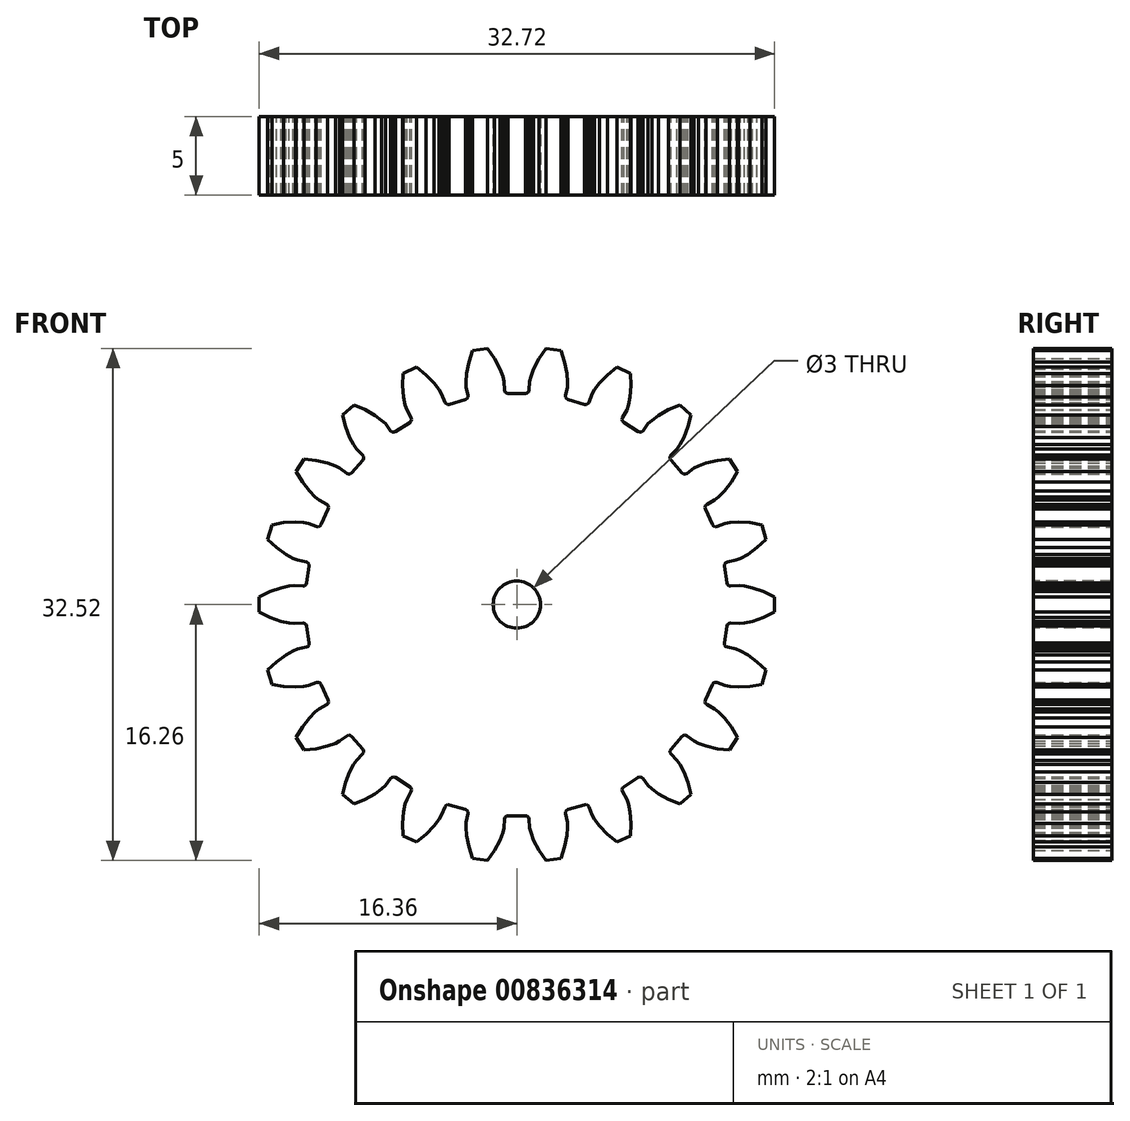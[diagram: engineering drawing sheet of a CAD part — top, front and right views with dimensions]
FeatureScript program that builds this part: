
annotation { "Feature Type Name" : "Feature", "Feature Type Description" : "" }
export const myFeature = defineFeature(function(context is Context, id is Id, definition is map)
    precondition{}
    {
        {
            var Q0;
            Q0=qCreatedBy(makeId("Front.planeOp"),FACE);
            var sketch = newSketch(context, id + "F0", { "sketchPlane" : qUnion([Q0])});
            skLineSegment(sketch, "E0", {"start": v(3.19, -14.67) * mm, "end": v(3.23, -14.15) * mm});
            skLineSegment(sketch, "E1", {"start": v(1.85, 16.26) * mm, "end": v(1.42, 15.62) * mm});
            skLineSegment(sketch, "E2", {"start": v(3.1, 13.28) * mm, "end": v(3.22, 13.83) * mm});
            skLineSegment(sketch, "E3", {"start": v(5.25, 14.06) * mm, "end": v(4.93, 13.65) * mm});
            skLineSegment(sketch, "E4", {"start": v(-9, -12.02) * mm, "end": v(-8.58, -11.7) * mm});
            skLineSegment(sketch, "E5", {"start": v(6.8, -11.58) * mm, "end": v(7.7, -10.99) * mm});
            skLineSegment(sketch, "E6", {"start": v(14.2, -2.94) * mm, "end": v(13.92, -2.82) * mm});
            skLineSegment(sketch, "E7", {"start": v(-0.54, 13.41) * mm, "end": v(-0.65, 13.44) * mm});
            skLineSegment(sketch, "E8", {"start": v(0.54, 13.41) * mm, "end": v(-0.54, 13.41) * mm});
            skLineSegment(sketch, "E9", {"start": v(-0.81, 14.18) * mm, "end": v(-0.89, 14.48) * mm});
            skLineSegment(sketch, "E10", {"start": v(-0.65, 13.44) * mm, "end": v(-0.74, 13.5) * mm});
            skLineSegment(sketch, "E11", {"start": v(-6.71, 11.66) * mm, "end": v(-6.8, 11.58) * mm});
            skLineSegment(sketch, "E12", {"start": v(0.81, 14.18) * mm, "end": v(0.77, 13.61) * mm});
            skLineSegment(sketch, "E13", {"start": v(-9.73, -9.3) * mm, "end": v(-9.73, -9.4) * mm});
            skLineSegment(sketch, "E14", {"start": v(3.1, 13.17) * mm, "end": v(3.1, 13.28) * mm});
            skLineSegment(sketch, "E15", {"start": v(4.57, 12.85) * mm, "end": v(4.51, 12.75) * mm});
            skLineSegment(sketch, "E16", {"start": v(0.89, 14.48) * mm, "end": v(0.81, 14.18) * mm});
            skLineSegment(sketch, "E17", {"start": v(-7.23, -14.68) * mm, "end": v(-6.36, -15.08) * mm});
            skLineSegment(sketch, "E18", {"start": v(-8.58, -11.7) * mm, "end": v(-8.35, -11.49) * mm});
            skLineSegment(sketch, "E19", {"start": v(-1.42, 15.62) * mm, "end": v(-1.85, 16.26) * mm});
            skLineSegment(sketch, "E20", {"start": v(-5.25, -14.06) * mm, "end": v(-4.93, -13.65) * mm});
            skLineSegment(sketch, "E21", {"start": v(3.04, 15.4) * mm, "end": v(2.8, 16.12) * mm});
            skLineSegment(sketch, "E22", {"start": v(-0.74, 13.5) * mm, "end": v(-0.77, 13.61) * mm});
            skLineSegment(sketch, "E23", {"start": v(14.07, -5.24) * mm, "end": v(14.8, -5.2) * mm});
            skLineSegment(sketch, "E24", {"start": v(-4.51, -12.75) * mm, "end": v(-4.41, -12.7) * mm});
            skLineSegment(sketch, "E25", {"start": v(-12.06, -6.36) * mm, "end": v(-12.56, -6.63) * mm});
            skLineSegment(sketch, "E26", {"start": v(-13.4, 1.27) * mm, "end": v(-13.48, 1.2) * mm});
            skLineSegment(sketch, "E27", {"start": v(-0.77, 13.61) * mm, "end": v(-0.81, 14.18) * mm});
            skLineSegment(sketch, "E28", {"start": v(-1.08, 14.97) * mm, "end": v(-1.42, 15.62) * mm});
            skLineSegment(sketch, "E29", {"start": v(-8, -11.04) * mm, "end": v(-7.92, -10.97) * mm});
            skLineSegment(sketch, "E30", {"start": v(-6.8, -11.58) * mm, "end": v(-6.71, -11.66) * mm});
            skLineSegment(sketch, "E31", {"start": v(-14.67, 3.2) * mm, "end": v(-14.2, 2.94) * mm});
            skLineSegment(sketch, "E32", {"start": v(-3.19, -14.67) * mm, "end": v(-3.04, -15.4) * mm});
            skLineSegment(sketch, "E33", {"start": v(0.54, -13.41) * mm, "end": v(0.65, -13.44) * mm});
            skLineSegment(sketch, "E34", {"start": v(-15.26, 3.63) * mm, "end": v(-14.67, 3.2) * mm});
            skLineSegment(sketch, "E35", {"start": v(-13.23, 5.15) * mm, "end": v(-13.54, 5.2) * mm});
            skLineSegment(sketch, "E36", {"start": v(-4.93, -13.65) * mm, "end": v(-4.77, -13.37) * mm});
            skLineSegment(sketch, "E37", {"start": v(-12.06, 6.36) * mm, "end": v(-11.98, 6.28) * mm});
            skLineSegment(sketch, "E38", {"start": v(-16.36, 0.48) * mm, "end": v(-16.36, -0.48) * mm});
            skLineSegment(sketch, "E39", {"start": v(-15.67, 0.82) * mm, "end": v(-16.36, 0.48) * mm});
            skLineSegment(sketch, "E40", {"start": v(3.19, 14.67) * mm, "end": v(3.04, 15.4) * mm});
            skLineSegment(sketch, "E41", {"start": v(3.23, 14.15) * mm, "end": v(3.19, 14.67) * mm});
            skLineSegment(sketch, "E42", {"start": v(3.22, 13.83) * mm, "end": v(3.23, 14.15) * mm});
            skLineSegment(sketch, "E43", {"start": v(-14.02, -8.44) * mm, "end": v(-13.5, -9.25) * mm});
            skLineSegment(sketch, "E44", {"start": v(-13.62, -7.78) * mm, "end": v(-14.02, -8.44) * mm});
            skLineSegment(sketch, "E45", {"start": v(-3.16, 13.08) * mm, "end": v(-3.26, 13.02) * mm});
            skLineSegment(sketch, "E46", {"start": v(-3.1, 13.17) * mm, "end": v(-3.16, 13.08) * mm});
            skLineSegment(sketch, "E47", {"start": v(-3.1, 13.28) * mm, "end": v(-3.1, 13.17) * mm});
            skLineSegment(sketch, "E48", {"start": v(-3.22, 13.83) * mm, "end": v(-3.1, 13.28) * mm});
            skLineSegment(sketch, "E49", {"start": v(-3.23, 14.15) * mm, "end": v(-3.22, 13.83) * mm});
            skLineSegment(sketch, "E50", {"start": v(-3.19, 14.67) * mm, "end": v(-3.23, 14.15) * mm});
            skLineSegment(sketch, "E51", {"start": v(-3.04, 15.4) * mm, "end": v(-3.19, 14.67) * mm});
            skLineSegment(sketch, "E52", {"start": v(-2.8, 16.12) * mm, "end": v(-3.04, 15.4) * mm});
            skLineSegment(sketch, "E53", {"start": v(-1.85, 16.26) * mm, "end": v(-2.8, 16.12) * mm});
            skLineSegment(sketch, "E54", {"start": v(5.76, 14.6) * mm, "end": v(5.25, 14.06) * mm});
            skLineSegment(sketch, "E55", {"start": v(6.36, 15.08) * mm, "end": v(5.76, 14.6) * mm});
            skLineSegment(sketch, "E56", {"start": v(7.23, 14.68) * mm, "end": v(6.36, 15.08) * mm});
            skLineSegment(sketch, "E57", {"start": v(-7.2, 13.18) * mm, "end": v(-7.08, 12.66) * mm});
            skLineSegment(sketch, "E58", {"start": v(-7.25, 13.91) * mm, "end": v(-7.2, 13.18) * mm});
            skLineSegment(sketch, "E59", {"start": v(-7.23, 14.68) * mm, "end": v(-7.25, 13.91) * mm});
            skLineSegment(sketch, "E60", {"start": v(-6.36, 15.08) * mm, "end": v(-7.23, 14.68) * mm});
            skLineSegment(sketch, "E61", {"start": v(-5.76, 14.6) * mm, "end": v(-6.36, 15.08) * mm});
            skLineSegment(sketch, "E62", {"start": v(-5.25, 14.06) * mm, "end": v(-5.76, 14.6) * mm});
            skLineSegment(sketch, "E63", {"start": v(-4.93, 13.65) * mm, "end": v(-5.25, 14.06) * mm});
            skLineSegment(sketch, "E64", {"start": v(-4.77, 13.37) * mm, "end": v(-4.93, 13.65) * mm});
            skLineSegment(sketch, "E65", {"start": v(-4.57, 12.85) * mm, "end": v(-4.77, 13.37) * mm});
            skLineSegment(sketch, "E66", {"start": v(-4.51, 12.75) * mm, "end": v(-4.57, 12.85) * mm});
            skLineSegment(sketch, "E67", {"start": v(1.42, 15.62) * mm, "end": v(1.08, 14.97) * mm});
            skLineSegment(sketch, "E68", {"start": v(-13.54, 5.2) * mm, "end": v(-14.07, 5.24) * mm});
            skLineSegment(sketch, "E69", {"start": v(-0.89, 14.48) * mm, "end": v(-1.08, 14.97) * mm});
            skLineSegment(sketch, "E70", {"start": v(13.17, -7.2) * mm, "end": v(12.8, -6.82) * mm});
            skLineSegment(sketch, "E71", {"start": v(2.8, 16.12) * mm, "end": v(1.85, 16.26) * mm});
            skLineSegment(sketch, "E72", {"start": v(-2.8, -16.12) * mm, "end": v(-1.85, -16.26) * mm});
            skLineSegment(sketch, "E73", {"start": v(-11.97, -6.07) * mm, "end": v(-11.95, -6.17) * mm});
            skLineSegment(sketch, "E74", {"start": v(-6.71, -11.87) * mm, "end": v(-6.98, -12.36) * mm});
            skLineSegment(sketch, "E75", {"start": v(-14.46, 1.18) * mm, "end": v(-14.97, 1.07) * mm});
            skLineSegment(sketch, "E76", {"start": v(-14.07, 5.24) * mm, "end": v(-14.8, 5.2) * mm});
            skLineSegment(sketch, "E77", {"start": v(-1.85, -16.26) * mm, "end": v(-1.42, -15.62) * mm});
            skLineSegment(sketch, "E78", {"start": v(-6.36, -15.08) * mm, "end": v(-5.76, -14.6) * mm});
            skLineSegment(sketch, "E79", {"start": v(-4.3, -12.72) * mm, "end": v(-4.41, -12.7) * mm});
            skLineSegment(sketch, "E80", {"start": v(-7.7, -10.99) * mm, "end": v(-7.81, -10.95) * mm});
            skLineSegment(sketch, "E81", {"start": v(7.23, 14.68) * mm, "end": v(7.25, 13.91) * mm});
            skLineSegment(sketch, "E82", {"start": v(0.74, -13.5) * mm, "end": v(0.77, -13.61) * mm});
            skLineSegment(sketch, "E83", {"start": v(-15.56, 5.07) * mm, "end": v(-14.8, 5.2) * mm});
            skLineSegment(sketch, "E84", {"start": v(-3.22, -13.83) * mm, "end": v(-3.23, -14.15) * mm});
            skLineSegment(sketch, "E85", {"start": v(-15.56, 5.07) * mm, "end": v(-15.83, 4.15) * mm});
            skLineSegment(sketch, "E86", {"start": v(-12.8, -6.82) * mm, "end": v(-13.17, -7.2) * mm});
            skLineSegment(sketch, "E87", {"start": v(-13.23, 5.15) * mm, "end": v(-12.7, 4.96) * mm});
            skLineSegment(sketch, "E88", {"start": v(-5.25, -14.06) * mm, "end": v(-5.76, -14.6) * mm});
            skLineSegment(sketch, "E89", {"start": v(-15.26, 3.63) * mm, "end": v(-15.83, 4.15) * mm});
            skLineSegment(sketch, "E90", {"start": v(13.5, -9.25) * mm, "end": v(12.74, -9.16) * mm});
            skLineSegment(sketch, "E91", {"start": v(-13.2, -2.56) * mm, "end": v(-13.27, -2.65) * mm});
            skLineSegment(sketch, "E92", {"start": v(-12.8, -6.82) * mm, "end": v(-12.56, -6.63) * mm});
            skLineSegment(sketch, "E93", {"start": v(-13.48, -1.2) * mm, "end": v(-13.59, -1.18) * mm});
            skLineSegment(sketch, "E94", {"start": v(-3.16, -13.08) * mm, "end": v(-3.1, -13.17) * mm});
            skLineSegment(sketch, "E95", {"start": v(-0.89, -14.48) * mm, "end": v(-1.08, -14.97) * mm});
            skLineSegment(sketch, "E96", {"start": v(11.53, -8.81) * mm, "end": v(11.24, -8.67) * mm});
            skLineSegment(sketch, "E97", {"start": v(-12.02, -9) * mm, "end": v(-12.74, -9.16) * mm});
            skLineSegment(sketch, "E98", {"start": v(-7.81, -10.95) * mm, "end": v(-7.92, -10.97) * mm});
            skLineSegment(sketch, "E99", {"start": v(-0.54, -13.41) * mm, "end": v(-0.65, -13.44) * mm});
            skLineSegment(sketch, "E100", {"start": v(9.64, -12.38) * mm, "end": v(9, -12.02) * mm});
            skLineSegment(sketch, "E101", {"start": v(-3.1, -13.28) * mm, "end": v(-3.22, -13.83) * mm});
            skLineSegment(sketch, "E102", {"start": v(-3.04, -15.4) * mm, "end": v(-2.8, -16.12) * mm});
            skLineSegment(sketch, "E103", {"start": v(-1.42, -15.62) * mm, "end": v(-1.08, -14.97) * mm});
            skLineSegment(sketch, "E104", {"start": v(-0.89, -14.48) * mm, "end": v(-0.81, -14.18) * mm});
            skLineSegment(sketch, "E105", {"start": v(-0.81, -14.18) * mm, "end": v(-0.77, -13.61) * mm});
            skLineSegment(sketch, "E106", {"start": v(-0.77, -13.61) * mm, "end": v(-0.74, -13.5) * mm});
            skLineSegment(sketch, "E107", {"start": v(-0.74, -13.5) * mm, "end": v(-0.65, -13.44) * mm});
            skLineSegment(sketch, "E108", {"start": v(-0.54, -13.41) * mm, "end": v(0.54, -13.41) * mm});
            skLineSegment(sketch, "E109", {"start": v(0.65, -13.44) * mm, "end": v(0.74, -13.5) * mm});
            skLineSegment(sketch, "E110", {"start": v(0.77, -13.61) * mm, "end": v(0.81, -14.18) * mm});
            skLineSegment(sketch, "E111", {"start": v(0.81, -14.18) * mm, "end": v(0.89, -14.48) * mm});
            skLineSegment(sketch, "E112", {"start": v(0.89, -14.48) * mm, "end": v(1.08, -14.97) * mm});
            skLineSegment(sketch, "E113", {"start": v(1.08, -14.97) * mm, "end": v(1.42, -15.62) * mm});
            skLineSegment(sketch, "E114", {"start": v(1.42, -15.62) * mm, "end": v(1.85, -16.26) * mm});
            skLineSegment(sketch, "E115", {"start": v(-15.26, -3.63) * mm, "end": v(-15.83, -4.15) * mm});
            skLineSegment(sketch, "E116", {"start": v(-15.83, -4.15) * mm, "end": v(-15.56, -5.07) * mm});
            skLineSegment(sketch, "E117", {"start": v(-15.56, -5.07) * mm, "end": v(-14.8, -5.2) * mm});
            skLineSegment(sketch, "E118", {"start": v(-14.67, -3.2) * mm, "end": v(-15.26, -3.63) * mm});
            skLineSegment(sketch, "E119", {"start": v(-14.8, -5.2) * mm, "end": v(-14.07, -5.24) * mm});
            skLineSegment(sketch, "E120", {"start": v(-14.2, -2.94) * mm, "end": v(-14.67, -3.2) * mm});
            skLineSegment(sketch, "E121", {"start": v(-13.92, -2.82) * mm, "end": v(-14.2, -2.94) * mm});
            skLineSegment(sketch, "E122", {"start": v(-14.07, -5.24) * mm, "end": v(-13.54, -5.2) * mm});
            skLineSegment(sketch, "E123", {"start": v(-13.37, -2.7) * mm, "end": v(-13.92, -2.82) * mm});
            skLineSegment(sketch, "E124", {"start": v(-13.54, -5.2) * mm, "end": v(-13.23, -5.15) * mm});
            skLineSegment(sketch, "E125", {"start": v(-13.27, -2.65) * mm, "end": v(-13.37, -2.7) * mm});
            skLineSegment(sketch, "E126", {"start": v(-13.23, -5.15) * mm, "end": v(-12.7, -4.96) * mm});
            skLineSegment(sketch, "E127", {"start": v(-13.2, -2.45) * mm, "end": v(-13.2, -2.56) * mm});
            skLineSegment(sketch, "E128", {"start": v(-13.17, -7.2) * mm, "end": v(-13.62, -7.78) * mm});
            skLineSegment(sketch, "E129", {"start": v(-13.5, -9.25) * mm, "end": v(-12.74, -9.16) * mm});
            skLineSegment(sketch, "E130", {"start": v(-11.98, -6.28) * mm, "end": v(-12.06, -6.36) * mm});
            skLineSegment(sketch, "E131", {"start": v(-12.02, -9) * mm, "end": v(-11.53, -8.81) * mm});
            skLineSegment(sketch, "E132", {"start": v(-11.95, -6.17) * mm, "end": v(-11.98, -6.28) * mm});
            skLineSegment(sketch, "E133", {"start": v(-10.88, -11.3) * mm, "end": v(-11.08, -12.05) * mm});
            skLineSegment(sketch, "E134", {"start": v(-11.08, -12.05) * mm, "end": v(-10.35, -12.68) * mm});
            skLineSegment(sketch, "E135", {"start": v(-10.61, -10.62) * mm, "end": v(-10.88, -11.3) * mm});
            skLineSegment(sketch, "E136", {"start": v(-10.36, -10.15) * mm, "end": v(-10.61, -10.62) * mm});
            skLineSegment(sketch, "E137", {"start": v(-10.18, -9.9) * mm, "end": v(-10.36, -10.15) * mm});
            skLineSegment(sketch, "E138", {"start": v(-10.35, -12.68) * mm, "end": v(-9.64, -12.38) * mm});
            skLineSegment(sketch, "E139", {"start": v(-9.79, -9.5) * mm, "end": v(-10.18, -9.9) * mm});
            skLineSegment(sketch, "E140", {"start": v(-9.73, -9.4) * mm, "end": v(-9.79, -9.5) * mm});
            skLineSegment(sketch, "E141", {"start": v(-7.2, -13.18) * mm, "end": v(-7.25, -13.91) * mm});
            skLineSegment(sketch, "E142", {"start": v(-7.25, -13.91) * mm, "end": v(-7.23, -14.68) * mm});
            skLineSegment(sketch, "E143", {"start": v(-7.08, -12.66) * mm, "end": v(-7.2, -13.18) * mm});
            skLineSegment(sketch, "E144", {"start": v(-6.98, -12.36) * mm, "end": v(-7.08, -12.66) * mm});
            skLineSegment(sketch, "E145", {"start": v(-6.69, -11.76) * mm, "end": v(-6.71, -11.87) * mm});
            skLineSegment(sketch, "E146", {"start": v(-3.23, -14.15) * mm, "end": v(-3.19, -14.67) * mm});
            skLineSegment(sketch, "E147", {"start": v(-7.08, 12.66) * mm, "end": v(-6.98, 12.36) * mm});
            skLineSegment(sketch, "E148", {"start": v(-6.98, 12.36) * mm, "end": v(-6.71, 11.87) * mm});
            skLineSegment(sketch, "E149", {"start": v(-6.71, 11.87) * mm, "end": v(-6.69, 11.76) * mm});
            skLineSegment(sketch, "E150", {"start": v(-4.77, -13.37) * mm, "end": v(-4.57, -12.85) * mm});
            skLineSegment(sketch, "E151", {"start": v(-4.57, -12.85) * mm, "end": v(-4.51, -12.75) * mm});
            skLineSegment(sketch, "E152", {"start": v(-4.41, 12.7) * mm, "end": v(-4.51, 12.75) * mm});
            skLineSegment(sketch, "E153", {"start": v(-4.3, 12.72) * mm, "end": v(-4.41, 12.7) * mm});
            skLineSegment(sketch, "E154", {"start": v(-4.3, -12.72) * mm, "end": v(-3.26, -13.02) * mm});
            skLineSegment(sketch, "E155", {"start": v(-3.26, 13.02) * mm, "end": v(-4.3, 12.72) * mm});
            skLineSegment(sketch, "E156", {"start": v(-3.26, -13.02) * mm, "end": v(-3.16, -13.08) * mm});
            skLineSegment(sketch, "E157", {"start": v(-3.1, -13.17) * mm, "end": v(-3.1, -13.28) * mm});
            skLineSegment(sketch, "E158", {"start": v(-10.35, 12.68) * mm, "end": v(-11.08, 12.05) * mm});
            skLineSegment(sketch, "E159", {"start": v(-11.08, 12.05) * mm, "end": v(-10.88, 11.3) * mm});
            skLineSegment(sketch, "E160", {"start": v(-10.88, 11.3) * mm, "end": v(-10.61, 10.62) * mm});
            skLineSegment(sketch, "E161", {"start": v(-10.61, 10.62) * mm, "end": v(-10.36, 10.15) * mm});
            skLineSegment(sketch, "E162", {"start": v(-10.36, 10.15) * mm, "end": v(-10.18, 9.9) * mm});
            skLineSegment(sketch, "E163", {"start": v(-9.64, 12.38) * mm, "end": v(-10.35, 12.68) * mm});
            skLineSegment(sketch, "E164", {"start": v(-10.18, 9.9) * mm, "end": v(-9.79, 9.5) * mm});
            skLineSegment(sketch, "E165", {"start": v(-9.79, 9.5) * mm, "end": v(-9.73, 9.4) * mm});
            skLineSegment(sketch, "E166", {"start": v(-9.73, 9.4) * mm, "end": v(-9.73, 9.3) * mm});
            skLineSegment(sketch, "E167", {"start": v(-9.64, -12.38) * mm, "end": v(-9, -12.02) * mm});
            skLineSegment(sketch, "E168", {"start": v(-9, 12.02) * mm, "end": v(-9.64, 12.38) * mm});
            skLineSegment(sketch, "E169", {"start": v(-8.58, 11.7) * mm, "end": v(-9, 12.02) * mm});
            skLineSegment(sketch, "E170", {"start": v(-8.35, 11.49) * mm, "end": v(-8.58, 11.7) * mm});
            skLineSegment(sketch, "E171", {"start": v(-8.35, -11.49) * mm, "end": v(-8, -11.04) * mm});
            skLineSegment(sketch, "E172", {"start": v(-8, 11.04) * mm, "end": v(-8.35, 11.49) * mm});
            skLineSegment(sketch, "E173", {"start": v(-7.92, 10.97) * mm, "end": v(-8, 11.04) * mm});
            skLineSegment(sketch, "E174", {"start": v(-7.81, 10.95) * mm, "end": v(-7.92, 10.97) * mm});
            skLineSegment(sketch, "E175", {"start": v(-7.7, 10.99) * mm, "end": v(-7.81, 10.95) * mm});
            skLineSegment(sketch, "E176", {"start": v(-7.7, -10.99) * mm, "end": v(-6.8, -11.58) * mm});
            skLineSegment(sketch, "E177", {"start": v(-6.8, 11.58) * mm, "end": v(-7.7, 10.99) * mm});
            skLineSegment(sketch, "E178", {"start": v(-6.71, -11.66) * mm, "end": v(-6.69, -11.76) * mm});
            skLineSegment(sketch, "E179", {"start": v(-6.69, 11.76) * mm, "end": v(-6.71, 11.66) * mm});
            skLineSegment(sketch, "E180", {"start": v(-13.5, 9.25) * mm, "end": v(-14.02, 8.44) * mm});
            skLineSegment(sketch, "E181", {"start": v(-14.02, 8.44) * mm, "end": v(-13.62, 7.78) * mm});
            skLineSegment(sketch, "E182", {"start": v(-13.62, 7.78) * mm, "end": v(-13.17, 7.2) * mm});
            skLineSegment(sketch, "E183", {"start": v(-12.74, 9.16) * mm, "end": v(-13.5, 9.25) * mm});
            skLineSegment(sketch, "E184", {"start": v(-13.17, 7.2) * mm, "end": v(-12.8, 6.82) * mm});
            skLineSegment(sketch, "E185", {"start": v(-12.8, 6.82) * mm, "end": v(-12.56, 6.63) * mm});
            skLineSegment(sketch, "E186", {"start": v(-12.02, 9) * mm, "end": v(-12.74, 9.16) * mm});
            skLineSegment(sketch, "E187", {"start": v(-12.56, 6.63) * mm, "end": v(-12.06, 6.36) * mm});
            skLineSegment(sketch, "E188", {"start": v(-11.53, 8.81) * mm, "end": v(-12.02, 9) * mm});
            skLineSegment(sketch, "E189", {"start": v(-11.98, 6.28) * mm, "end": v(-11.95, 6.17) * mm});
            skLineSegment(sketch, "E190", {"start": v(-11.53, -8.81) * mm, "end": v(-11.24, -8.67) * mm});
            skLineSegment(sketch, "E191", {"start": v(-11.24, 8.67) * mm, "end": v(-11.53, 8.81) * mm});
            skLineSegment(sketch, "E192", {"start": v(-11.24, -8.67) * mm, "end": v(-10.8, -8.33) * mm});
            skLineSegment(sketch, "E193", {"start": v(-10.8, 8.33) * mm, "end": v(-11.24, 8.67) * mm});
            skLineSegment(sketch, "E194", {"start": v(-10.8, -8.33) * mm, "end": v(-10.7, -8.3) * mm});
            skLineSegment(sketch, "E195", {"start": v(-10.7, 8.3) * mm, "end": v(-10.8, 8.33) * mm});
            skLineSegment(sketch, "E196", {"start": v(-10.7, -8.3) * mm, "end": v(-10.58, -8.3) * mm});
            skLineSegment(sketch, "E197", {"start": v(-10.58, 8.3) * mm, "end": v(-10.7, 8.3) * mm});
            skLineSegment(sketch, "E198", {"start": v(-10.58, -8.3) * mm, "end": v(-10.5, -8.37) * mm});
            skLineSegment(sketch, "E199", {"start": v(-10.5, 8.37) * mm, "end": v(-10.58, 8.3) * mm});
            skLineSegment(sketch, "E200", {"start": v(-10.5, -8.37) * mm, "end": v(-9.78, -9.2) * mm});
            skLineSegment(sketch, "E201", {"start": v(-9.78, 9.2) * mm, "end": v(-10.5, 8.37) * mm});
            skLineSegment(sketch, "E202", {"start": v(-9.78, -9.2) * mm, "end": v(-9.73, -9.3) * mm});
            skLineSegment(sketch, "E203", {"start": v(-9.73, 9.3) * mm, "end": v(-9.78, 9.2) * mm});
            skLineSegment(sketch, "E204", {"start": v(-14.2, 2.94) * mm, "end": v(-13.92, 2.82) * mm});
            skLineSegment(sketch, "E205", {"start": v(-13.92, 2.82) * mm, "end": v(-13.37, 2.7) * mm});
            skLineSegment(sketch, "E206", {"start": v(-13.37, 2.7) * mm, "end": v(-13.27, 2.65) * mm});
            skLineSegment(sketch, "E207", {"start": v(-13.27, 2.65) * mm, "end": v(-13.2, 2.56) * mm});
            skLineSegment(sketch, "E208", {"start": v(-13.2, 2.56) * mm, "end": v(-13.2, 2.45) * mm});
            skLineSegment(sketch, "E209", {"start": v(-12.7, -4.96) * mm, "end": v(-12.6, -4.94) * mm});
            skLineSegment(sketch, "E210", {"start": v(-12.6, 4.94) * mm, "end": v(-12.7, 4.96) * mm});
            skLineSegment(sketch, "E211", {"start": v(-12.6, -4.94) * mm, "end": v(-12.5, -4.99) * mm});
            skLineSegment(sketch, "E212", {"start": v(-12.5, 4.99) * mm, "end": v(-12.6, 4.94) * mm});
            skLineSegment(sketch, "E213", {"start": v(-12.5, -4.99) * mm, "end": v(-12.43, -5.08) * mm});
            skLineSegment(sketch, "E214", {"start": v(-12.43, 5.08) * mm, "end": v(-12.5, 4.99) * mm});
            skLineSegment(sketch, "E215", {"start": v(-12.43, -5.08) * mm, "end": v(-11.97, -6.07) * mm});
            skLineSegment(sketch, "E216", {"start": v(-11.97, 6.07) * mm, "end": v(-12.43, 5.08) * mm});
            skLineSegment(sketch, "E217", {"start": v(-11.95, 6.17) * mm, "end": v(-11.97, 6.07) * mm});
            skLineSegment(sketch, "E218", {"start": v(-16.36, -0.48) * mm, "end": v(-15.67, -0.82) * mm});
            skLineSegment(sketch, "E219", {"start": v(-15.67, -0.82) * mm, "end": v(-14.97, -1.07) * mm});
            skLineSegment(sketch, "E220", {"start": v(-14.97, 1.07) * mm, "end": v(-15.67, 0.82) * mm});
            skLineSegment(sketch, "E221", {"start": v(-14.97, -1.07) * mm, "end": v(-14.46, -1.18) * mm});
            skLineSegment(sketch, "E222", {"start": v(-14.46, -1.18) * mm, "end": v(-14.15, -1.22) * mm});
            skLineSegment(sketch, "E223", {"start": v(-14.15, 1.22) * mm, "end": v(-14.46, 1.18) * mm});
            skLineSegment(sketch, "E224", {"start": v(-14.15, -1.22) * mm, "end": v(-13.59, -1.18) * mm});
            skLineSegment(sketch, "E225", {"start": v(-13.59, 1.18) * mm, "end": v(-14.15, 1.22) * mm});
            skLineSegment(sketch, "E226", {"start": v(-13.48, 1.2) * mm, "end": v(-13.59, 1.18) * mm});
            skLineSegment(sketch, "E227", {"start": v(-13.48, -1.2) * mm, "end": v(-13.4, -1.27) * mm});
            skLineSegment(sketch, "E228", {"start": v(-13.4, -1.27) * mm, "end": v(-13.35, -1.37) * mm});
            skLineSegment(sketch, "E229", {"start": v(-13.35, 1.37) * mm, "end": v(-13.4, 1.27) * mm});
            skLineSegment(sketch, "E230", {"start": v(-13.35, -1.37) * mm, "end": v(-13.2, -2.45) * mm});
            skLineSegment(sketch, "E231", {"start": v(-13.2, 2.45) * mm, "end": v(-13.35, 1.37) * mm});
            skLineSegment(sketch, "E232", {"start": v(0.65, 13.44) * mm, "end": v(0.54, 13.41) * mm});
            skLineSegment(sketch, "E233", {"start": v(0.74, 13.5) * mm, "end": v(0.65, 13.44) * mm});
            skLineSegment(sketch, "E234", {"start": v(0.77, 13.61) * mm, "end": v(0.74, 13.5) * mm});
            skLineSegment(sketch, "E235", {"start": v(1.08, 14.97) * mm, "end": v(0.89, 14.48) * mm});
            skLineSegment(sketch, "E236", {"start": v(1.85, -16.26) * mm, "end": v(2.8, -16.12) * mm});
            skLineSegment(sketch, "E237", {"start": v(2.8, -16.12) * mm, "end": v(3.04, -15.4) * mm});
            skLineSegment(sketch, "E238", {"start": v(3.04, -15.4) * mm, "end": v(3.19, -14.67) * mm});
            skLineSegment(sketch, "E239", {"start": v(3.22, -13.83) * mm, "end": v(3.1, -13.28) * mm});
            skLineSegment(sketch, "E240", {"start": v(3.23, -14.15) * mm, "end": v(3.22, -13.83) * mm});
            skLineSegment(sketch, "E241", {"start": v(3.1, -13.28) * mm, "end": v(3.1, -13.17) * mm});
            skLineSegment(sketch, "E242", {"start": v(3.1, -13.17) * mm, "end": v(3.16, -13.08) * mm});
            skLineSegment(sketch, "E243", {"start": v(3.16, 13.08) * mm, "end": v(3.1, 13.17) * mm});
            skLineSegment(sketch, "E244", {"start": v(3.16, -13.08) * mm, "end": v(3.26, -13.02) * mm});
            skLineSegment(sketch, "E245", {"start": v(3.26, 13.02) * mm, "end": v(3.16, 13.08) * mm});
            skLineSegment(sketch, "E246", {"start": v(3.26, -13.02) * mm, "end": v(4.3, -12.72) * mm});
            skLineSegment(sketch, "E247", {"start": v(4.3, 12.72) * mm, "end": v(3.26, 13.02) * mm});
            skLineSegment(sketch, "E248", {"start": v(4.3, -12.72) * mm, "end": v(4.41, -12.7) * mm});
            skLineSegment(sketch, "E249", {"start": v(4.41, 12.7) * mm, "end": v(4.3, 12.72) * mm});
            skLineSegment(sketch, "E250", {"start": v(4.41, -12.7) * mm, "end": v(4.51, -12.75) * mm});
            skLineSegment(sketch, "E251", {"start": v(4.51, 12.75) * mm, "end": v(4.41, 12.7) * mm});
            skLineSegment(sketch, "E252", {"start": v(4.51, -12.75) * mm, "end": v(4.57, -12.85) * mm});
            skLineSegment(sketch, "E253", {"start": v(4.57, -12.85) * mm, "end": v(4.77, -13.37) * mm});
            skLineSegment(sketch, "E254", {"start": v(4.77, 13.37) * mm, "end": v(4.57, 12.85) * mm});
            skLineSegment(sketch, "E255", {"start": v(4.77, -13.37) * mm, "end": v(4.93, -13.65) * mm});
            skLineSegment(sketch, "E256", {"start": v(4.93, 13.65) * mm, "end": v(4.77, 13.37) * mm});
            skLineSegment(sketch, "E257", {"start": v(4.93, -13.65) * mm, "end": v(5.25, -14.06) * mm});
            skLineSegment(sketch, "E258", {"start": v(5.25, -14.06) * mm, "end": v(5.76, -14.6) * mm});
            skLineSegment(sketch, "E259", {"start": v(5.76, -14.6) * mm, "end": v(6.36, -15.08) * mm});
            skLineSegment(sketch, "E260", {"start": v(6.36, -15.08) * mm, "end": v(7.23, -14.68) * mm});
            skLineSegment(sketch, "E261", {"start": v(6.71, -11.87) * mm, "end": v(6.69, -11.76) * mm});
            skLineSegment(sketch, "E262", {"start": v(6.98, -12.36) * mm, "end": v(6.71, -11.87) * mm});
            skLineSegment(sketch, "E263", {"start": v(7.08, -12.66) * mm, "end": v(6.98, -12.36) * mm});
            skLineSegment(sketch, "E264", {"start": v(7.2, -13.18) * mm, "end": v(7.08, -12.66) * mm});
            skLineSegment(sketch, "E265", {"start": v(7.23, -14.68) * mm, "end": v(7.25, -13.91) * mm});
            skLineSegment(sketch, "E266", {"start": v(7.25, -13.91) * mm, "end": v(7.2, -13.18) * mm});
            skLineSegment(sketch, "E267", {"start": v(6.69, -11.76) * mm, "end": v(6.71, -11.66) * mm});
            skLineSegment(sketch, "E268", {"start": v(6.71, 11.66) * mm, "end": v(6.69, 11.76) * mm});
            skLineSegment(sketch, "E269", {"start": v(6.71, -11.66) * mm, "end": v(6.8, -11.58) * mm});
            skLineSegment(sketch, "E270", {"start": v(6.8, 11.58) * mm, "end": v(6.71, 11.66) * mm});
            skLineSegment(sketch, "E271", {"start": v(7.7, 10.99) * mm, "end": v(6.8, 11.58) * mm});
            skLineSegment(sketch, "E272", {"start": v(7.7, -10.99) * mm, "end": v(7.81, -10.95) * mm});
            skLineSegment(sketch, "E273", {"start": v(7.81, 10.95) * mm, "end": v(7.7, 10.99) * mm});
            skLineSegment(sketch, "E274", {"start": v(7.81, -10.95) * mm, "end": v(7.92, -10.97) * mm});
            skLineSegment(sketch, "E275", {"start": v(7.92, 10.97) * mm, "end": v(7.81, 10.95) * mm});
            skLineSegment(sketch, "E276", {"start": v(7.92, -10.97) * mm, "end": v(8, -11.04) * mm});
            skLineSegment(sketch, "E277", {"start": v(8, 11.04) * mm, "end": v(7.92, 10.97) * mm});
            skLineSegment(sketch, "E278", {"start": v(8, -11.04) * mm, "end": v(8.35, -11.49) * mm});
            skLineSegment(sketch, "E279", {"start": v(8.35, 11.49) * mm, "end": v(8, 11.04) * mm});
            skLineSegment(sketch, "E280", {"start": v(8.35, -11.49) * mm, "end": v(8.58, -11.7) * mm});
            skLineSegment(sketch, "E281", {"start": v(8.58, 11.7) * mm, "end": v(8.35, 11.49) * mm});
            skLineSegment(sketch, "E282", {"start": v(8.58, -11.7) * mm, "end": v(9, -12.02) * mm});
            skLineSegment(sketch, "E283", {"start": v(9, 12.02) * mm, "end": v(8.58, 11.7) * mm});
            skLineSegment(sketch, "E284", {"start": v(9.64, 12.38) * mm, "end": v(9, 12.02) * mm});
            skLineSegment(sketch, "E285", {"start": v(9.73, -9.4) * mm, "end": v(9.73, -9.3) * mm});
            skLineSegment(sketch, "E286", {"start": v(9.64, -12.38) * mm, "end": v(10.35, -12.68) * mm});
            skLineSegment(sketch, "E287", {"start": v(9.79, -9.5) * mm, "end": v(9.73, -9.4) * mm});
            skLineSegment(sketch, "E288", {"start": v(10.18, -9.9) * mm, "end": v(9.79, -9.5) * mm});
            skLineSegment(sketch, "E289", {"start": v(10.36, -10.15) * mm, "end": v(10.18, -9.9) * mm});
            skLineSegment(sketch, "E290", {"start": v(10.35, -12.68) * mm, "end": v(11.08, -12.05) * mm});
            skLineSegment(sketch, "E291", {"start": v(10.61, -10.62) * mm, "end": v(10.36, -10.15) * mm});
            skLineSegment(sketch, "E292", {"start": v(11.08, -12.05) * mm, "end": v(10.88, -11.3) * mm});
            skLineSegment(sketch, "E293", {"start": v(10.88, -11.3) * mm, "end": v(10.61, -10.62) * mm});
            skLineSegment(sketch, "E294", {"start": v(9.73, -9.3) * mm, "end": v(9.78, -9.2) * mm});
            skLineSegment(sketch, "E295", {"start": v(9.78, 9.2) * mm, "end": v(9.73, 9.3) * mm});
            skLineSegment(sketch, "E296", {"start": v(9.78, -9.2) * mm, "end": v(10.5, -8.37) * mm});
            skLineSegment(sketch, "E297", {"start": v(10.5, 8.37) * mm, "end": v(9.78, 9.2) * mm});
            skLineSegment(sketch, "E298", {"start": v(10.5, -8.37) * mm, "end": v(10.58, -8.3) * mm});
            skLineSegment(sketch, "E299", {"start": v(10.58, 8.3) * mm, "end": v(10.5, 8.37) * mm});
            skLineSegment(sketch, "E300", {"start": v(10.58, -8.3) * mm, "end": v(10.7, -8.3) * mm});
            skLineSegment(sketch, "E301", {"start": v(10.7, 8.3) * mm, "end": v(10.58, 8.3) * mm});
            skLineSegment(sketch, "E302", {"start": v(10.7, -8.3) * mm, "end": v(10.8, -8.33) * mm});
            skLineSegment(sketch, "E303", {"start": v(10.8, 8.33) * mm, "end": v(10.7, 8.3) * mm});
            skLineSegment(sketch, "E304", {"start": v(10.8, -8.33) * mm, "end": v(11.24, -8.67) * mm});
            skLineSegment(sketch, "E305", {"start": v(11.24, 8.67) * mm, "end": v(10.8, 8.33) * mm});
            skLineSegment(sketch, "E306", {"start": v(11.53, 8.81) * mm, "end": v(11.24, 8.67) * mm});
            skLineSegment(sketch, "E307", {"start": v(11.53, -8.81) * mm, "end": v(12.02, -9) * mm});
            skLineSegment(sketch, "E308", {"start": v(11.98, -6.28) * mm, "end": v(11.95, -6.17) * mm});
            skLineSegment(sketch, "E309", {"start": v(12.06, -6.36) * mm, "end": v(11.98, -6.28) * mm});
            skLineSegment(sketch, "E310", {"start": v(12.02, -9) * mm, "end": v(12.74, -9.16) * mm});
            skLineSegment(sketch, "E311", {"start": v(12.56, -6.63) * mm, "end": v(12.06, -6.36) * mm});
            skLineSegment(sketch, "E312", {"start": v(12.8, -6.82) * mm, "end": v(12.56, -6.63) * mm});
            skLineSegment(sketch, "E313", {"start": v(13.62, -7.78) * mm, "end": v(13.17, -7.2) * mm});
            skLineSegment(sketch, "E314", {"start": v(13.5, -9.25) * mm, "end": v(14.02, -8.44) * mm});
            skLineSegment(sketch, "E315", {"start": v(14.02, -8.44) * mm, "end": v(13.62, -7.78) * mm});
            skLineSegment(sketch, "E316", {"start": v(11.95, -6.17) * mm, "end": v(11.97, -6.07) * mm});
            skLineSegment(sketch, "E317", {"start": v(11.97, 6.07) * mm, "end": v(11.95, 6.17) * mm});
            skLineSegment(sketch, "E318", {"start": v(11.97, -6.07) * mm, "end": v(12.43, -5.08) * mm});
            skLineSegment(sketch, "E319", {"start": v(12.43, 5.08) * mm, "end": v(11.97, 6.07) * mm});
            skLineSegment(sketch, "E320", {"start": v(12.43, -5.08) * mm, "end": v(12.5, -4.99) * mm});
            skLineSegment(sketch, "E321", {"start": v(12.5, 4.99) * mm, "end": v(12.43, 5.08) * mm});
            skLineSegment(sketch, "E322", {"start": v(12.5, -4.99) * mm, "end": v(12.6, -4.94) * mm});
            skLineSegment(sketch, "E323", {"start": v(12.6, 4.94) * mm, "end": v(12.5, 4.99) * mm});
            skLineSegment(sketch, "E324", {"start": v(12.6, -4.94) * mm, "end": v(12.7, -4.96) * mm});
            skLineSegment(sketch, "E325", {"start": v(12.7, 4.96) * mm, "end": v(12.6, 4.94) * mm});
            skLineSegment(sketch, "E326", {"start": v(12.7, -4.96) * mm, "end": v(13.23, -5.15) * mm});
            skLineSegment(sketch, "E327", {"start": v(13.2, -2.56) * mm, "end": v(13.2, -2.45) * mm});
            skLineSegment(sketch, "E328", {"start": v(13.27, -2.65) * mm, "end": v(13.2, -2.56) * mm});
            skLineSegment(sketch, "E329", {"start": v(13.23, -5.15) * mm, "end": v(13.54, -5.2) * mm});
            skLineSegment(sketch, "E330", {"start": v(13.37, -2.7) * mm, "end": v(13.27, -2.65) * mm});
            skLineSegment(sketch, "E331", {"start": v(13.92, -2.82) * mm, "end": v(13.37, -2.7) * mm});
            skLineSegment(sketch, "E332", {"start": v(13.54, -5.2) * mm, "end": v(14.07, -5.24) * mm});
            skLineSegment(sketch, "E333", {"start": v(14.67, -3.2) * mm, "end": v(14.2, -2.94) * mm});
            skLineSegment(sketch, "E334", {"start": v(15.26, -3.63) * mm, "end": v(14.67, -3.2) * mm});
            skLineSegment(sketch, "E335", {"start": v(14.8, -5.2) * mm, "end": v(15.56, -5.07) * mm});
            skLineSegment(sketch, "E336", {"start": v(15.56, -5.07) * mm, "end": v(15.83, -4.15) * mm});
            skLineSegment(sketch, "E337", {"start": v(15.83, -4.15) * mm, "end": v(15.26, -3.63) * mm});
            skLineSegment(sketch, "E338", {"start": v(13.2, -2.45) * mm, "end": v(13.35, -1.37) * mm});
            skLineSegment(sketch, "E339", {"start": v(13.35, 1.37) * mm, "end": v(13.2, 2.45) * mm});
            skLineSegment(sketch, "E340", {"start": v(13.35, -1.37) * mm, "end": v(13.4, -1.27) * mm});
            skLineSegment(sketch, "E341", {"start": v(13.4, 1.27) * mm, "end": v(13.35, 1.37) * mm});
            skLineSegment(sketch, "E342", {"start": v(13.4, -1.27) * mm, "end": v(13.48, -1.2) * mm});
            skLineSegment(sketch, "E343", {"start": v(13.48, 1.2) * mm, "end": v(13.4, 1.27) * mm});
            skLineSegment(sketch, "E344", {"start": v(13.59, 1.18) * mm, "end": v(13.48, 1.2) * mm});
            skLineSegment(sketch, "E345", {"start": v(13.48, -1.2) * mm, "end": v(13.59, -1.18) * mm});
            skLineSegment(sketch, "E346", {"start": v(13.59, -1.18) * mm, "end": v(14.15, -1.22) * mm});
            skLineSegment(sketch, "E347", {"start": v(14.15, 1.22) * mm, "end": v(13.59, 1.18) * mm});
            skLineSegment(sketch, "E348", {"start": v(14.46, 1.18) * mm, "end": v(14.15, 1.22) * mm});
            skLineSegment(sketch, "E349", {"start": v(14.15, -1.22) * mm, "end": v(14.46, -1.18) * mm});
            skLineSegment(sketch, "E350", {"start": v(14.46, -1.18) * mm, "end": v(14.97, -1.07) * mm});
            skLineSegment(sketch, "E351", {"start": v(14.97, 1.07) * mm, "end": v(14.46, 1.18) * mm});
            skLineSegment(sketch, "E352", {"start": v(14.97, -1.07) * mm, "end": v(15.67, -0.82) * mm});
            skLineSegment(sketch, "E353", {"start": v(15.67, 0.82) * mm, "end": v(14.97, 1.07) * mm});
            skLineSegment(sketch, "E354", {"start": v(15.67, -0.82) * mm, "end": v(16.36, -0.48) * mm});
            skLineSegment(sketch, "E355", {"start": v(16.36, -0.48) * mm, "end": v(16.36, 0.48) * mm});
            skLineSegment(sketch, "E356", {"start": v(16.36, 0.48) * mm, "end": v(15.67, 0.82) * mm});
            skLineSegment(sketch, "E357", {"start": v(13.23, 5.15) * mm, "end": v(12.7, 4.96) * mm});
            skLineSegment(sketch, "E358", {"start": v(13.2, 2.45) * mm, "end": v(13.2, 2.56) * mm});
            skLineSegment(sketch, "E359", {"start": v(13.2, 2.56) * mm, "end": v(13.27, 2.65) * mm});
            skLineSegment(sketch, "E360", {"start": v(13.54, 5.2) * mm, "end": v(13.23, 5.15) * mm});
            skLineSegment(sketch, "E361", {"start": v(13.27, 2.65) * mm, "end": v(13.37, 2.7) * mm});
            skLineSegment(sketch, "E362", {"start": v(13.37, 2.7) * mm, "end": v(13.92, 2.82) * mm});
            skLineSegment(sketch, "E363", {"start": v(14.07, 5.24) * mm, "end": v(13.54, 5.2) * mm});
            skLineSegment(sketch, "E364", {"start": v(13.92, 2.82) * mm, "end": v(14.2, 2.94) * mm});
            skLineSegment(sketch, "E365", {"start": v(14.8, 5.2) * mm, "end": v(14.07, 5.24) * mm});
            skLineSegment(sketch, "E366", {"start": v(14.2, 2.94) * mm, "end": v(14.67, 3.2) * mm});
            skLineSegment(sketch, "E367", {"start": v(14.67, 3.2) * mm, "end": v(15.26, 3.63) * mm});
            skLineSegment(sketch, "E368", {"start": v(15.56, 5.07) * mm, "end": v(14.8, 5.2) * mm});
            skLineSegment(sketch, "E369", {"start": v(15.26, 3.63) * mm, "end": v(15.83, 4.15) * mm});
            skLineSegment(sketch, "E370", {"start": v(15.83, 4.15) * mm, "end": v(15.56, 5.07) * mm});
            skLineSegment(sketch, "E371", {"start": v(12.02, 9) * mm, "end": v(11.53, 8.81) * mm});
            skLineSegment(sketch, "E372", {"start": v(11.95, 6.17) * mm, "end": v(11.98, 6.28) * mm});
            skLineSegment(sketch, "E373", {"start": v(11.98, 6.28) * mm, "end": v(12.06, 6.36) * mm});
            skLineSegment(sketch, "E374", {"start": v(12.74, 9.16) * mm, "end": v(12.02, 9) * mm});
            skLineSegment(sketch, "E375", {"start": v(12.06, 6.36) * mm, "end": v(12.56, 6.63) * mm});
            skLineSegment(sketch, "E376", {"start": v(12.56, 6.63) * mm, "end": v(12.8, 6.82) * mm});
            skLineSegment(sketch, "E377", {"start": v(13.5, 9.25) * mm, "end": v(12.74, 9.16) * mm});
            skLineSegment(sketch, "E378", {"start": v(12.8, 6.82) * mm, "end": v(13.17, 7.2) * mm});
            skLineSegment(sketch, "E379", {"start": v(13.17, 7.2) * mm, "end": v(13.62, 7.78) * mm});
            skLineSegment(sketch, "E380", {"start": v(13.62, 7.78) * mm, "end": v(14.02, 8.44) * mm});
            skLineSegment(sketch, "E381", {"start": v(14.02, 8.44) * mm, "end": v(13.5, 9.25) * mm});
            skLineSegment(sketch, "E382", {"start": v(10.35, 12.68) * mm, "end": v(9.64, 12.38) * mm});
            skLineSegment(sketch, "E383", {"start": v(9.73, 9.3) * mm, "end": v(9.73, 9.4) * mm});
            skLineSegment(sketch, "E384", {"start": v(9.73, 9.4) * mm, "end": v(9.79, 9.5) * mm});
            skLineSegment(sketch, "E385", {"start": v(9.79, 9.5) * mm, "end": v(10.18, 9.9) * mm});
            skLineSegment(sketch, "E386", {"start": v(10.18, 9.9) * mm, "end": v(10.36, 10.15) * mm});
            skLineSegment(sketch, "E387", {"start": v(11.08, 12.05) * mm, "end": v(10.35, 12.68) * mm});
            skLineSegment(sketch, "E388", {"start": v(10.36, 10.15) * mm, "end": v(10.61, 10.62) * mm});
            skLineSegment(sketch, "E389", {"start": v(10.61, 10.62) * mm, "end": v(10.88, 11.3) * mm});
            skLineSegment(sketch, "E390", {"start": v(10.88, 11.3) * mm, "end": v(11.08, 12.05) * mm});
            skLineSegment(sketch, "E391", {"start": v(6.69, 11.76) * mm, "end": v(6.71, 11.87) * mm});
            skLineSegment(sketch, "E392", {"start": v(6.71, 11.87) * mm, "end": v(6.98, 12.36) * mm});
            skLineSegment(sketch, "E393", {"start": v(6.98, 12.36) * mm, "end": v(7.08, 12.66) * mm});
            skLineSegment(sketch, "E394", {"start": v(7.08, 12.66) * mm, "end": v(7.2, 13.18) * mm});
            skLineSegment(sketch, "E395", {"start": v(7.2, 13.18) * mm, "end": v(7.25, 13.91) * mm});
            skSolve(sketch);
        }
        {
            var Q0;
            Q0 = qSketchRegion(id + "F0", true);
            extrude(context, id + "F1", {"entities" : qUnion([Q0]), "depth" : 5 * mm, "offsetDistance" : 25 * mm});
        }
        {
            var Q0;
            Q0=makeQuery(id+"F1.opExtrude","CAP_FACE",FACE,{"disambiguationData":[OSD([sQuery(id+"F0.wireOp",EDGE,"E0"),sQuery(id+"F0.wireOp",EDGE,"E1"),sQuery(id+"F0.wireOp",EDGE,"E2"),sQuery(id+"F0.wireOp",EDGE,"E3"),sQuery(id+"F0.wireOp",EDGE,"E4"),sQuery(id+"F0.wireOp",EDGE,"E5"),sQuery(id+"F0.wireOp",EDGE,"E6"),sQuery(id+"F0.wireOp",EDGE,"E7"),sQuery(id+"F0.wireOp",EDGE,"E8"),sQuery(id+"F0.wireOp",EDGE,"E9"),sQuery(id+"F0.wireOp",EDGE,"E10"),sQuery(id+"F0.wireOp",EDGE,"E11"),sQuery(id+"F0.wireOp",EDGE,"E12"),sQuery(id+"F0.wireOp",EDGE,"E13"),sQuery(id+"F0.wireOp",EDGE,"E14"),sQuery(id+"F0.wireOp",EDGE,"E15"),sQuery(id+"F0.wireOp",EDGE,"E16"),sQuery(id+"F0.wireOp",EDGE,"E17"),sQuery(id+"F0.wireOp",EDGE,"E18"),sQuery(id+"F0.wireOp",EDGE,"E19"),sQuery(id+"F0.wireOp",EDGE,"E20"),sQuery(id+"F0.wireOp",EDGE,"E21"),sQuery(id+"F0.wireOp",EDGE,"E22"),sQuery(id+"F0.wireOp",EDGE,"E23"),sQuery(id+"F0.wireOp",EDGE,"E24"),sQuery(id+"F0.wireOp",EDGE,"E25"),sQuery(id+"F0.wireOp",EDGE,"E26"),sQuery(id+"F0.wireOp",EDGE,"E27"),sQuery(id+"F0.wireOp",EDGE,"E28"),sQuery(id+"F0.wireOp",EDGE,"E29"),sQuery(id+"F0.wireOp",EDGE,"E30"),sQuery(id+"F0.wireOp",EDGE,"E31"),sQuery(id+"F0.wireOp",EDGE,"E32"),sQuery(id+"F0.wireOp",EDGE,"E33"),sQuery(id+"F0.wireOp",EDGE,"E34"),sQuery(id+"F0.wireOp",EDGE,"E35"),sQuery(id+"F0.wireOp",EDGE,"E36"),sQuery(id+"F0.wireOp",EDGE,"E37"),sQuery(id+"F0.wireOp",EDGE,"E38"),sQuery(id+"F0.wireOp",EDGE,"E39"),sQuery(id+"F0.wireOp",EDGE,"E40"),sQuery(id+"F0.wireOp",EDGE,"E41"),sQuery(id+"F0.wireOp",EDGE,"E42"),sQuery(id+"F0.wireOp",EDGE,"E43"),sQuery(id+"F0.wireOp",EDGE,"E44"),sQuery(id+"F0.wireOp",EDGE,"E45"),sQuery(id+"F0.wireOp",EDGE,"E46"),sQuery(id+"F0.wireOp",EDGE,"E47"),sQuery(id+"F0.wireOp",EDGE,"E48"),sQuery(id+"F0.wireOp",EDGE,"E49"),sQuery(id+"F0.wireOp",EDGE,"E50"),sQuery(id+"F0.wireOp",EDGE,"E51"),sQuery(id+"F0.wireOp",EDGE,"E52"),sQuery(id+"F0.wireOp",EDGE,"E53"),sQuery(id+"F0.wireOp",EDGE,"E54"),sQuery(id+"F0.wireOp",EDGE,"E55"),sQuery(id+"F0.wireOp",EDGE,"E56"),sQuery(id+"F0.wireOp",EDGE,"E57"),sQuery(id+"F0.wireOp",EDGE,"E58"),sQuery(id+"F0.wireOp",EDGE,"E59"),sQuery(id+"F0.wireOp",EDGE,"E60"),sQuery(id+"F0.wireOp",EDGE,"E61"),sQuery(id+"F0.wireOp",EDGE,"E62"),sQuery(id+"F0.wireOp",EDGE,"E63"),sQuery(id+"F0.wireOp",EDGE,"E64"),sQuery(id+"F0.wireOp",EDGE,"E65"),sQuery(id+"F0.wireOp",EDGE,"E66"),sQuery(id+"F0.wireOp",EDGE,"E67"),sQuery(id+"F0.wireOp",EDGE,"E68"),sQuery(id+"F0.wireOp",EDGE,"E69"),sQuery(id+"F0.wireOp",EDGE,"E70"),sQuery(id+"F0.wireOp",EDGE,"E71"),sQuery(id+"F0.wireOp",EDGE,"E72"),sQuery(id+"F0.wireOp",EDGE,"E73"),sQuery(id+"F0.wireOp",EDGE,"E74"),sQuery(id+"F0.wireOp",EDGE,"E75"),sQuery(id+"F0.wireOp",EDGE,"E76"),sQuery(id+"F0.wireOp",EDGE,"E77"),sQuery(id+"F0.wireOp",EDGE,"E78"),sQuery(id+"F0.wireOp",EDGE,"E79"),sQuery(id+"F0.wireOp",EDGE,"E80"),sQuery(id+"F0.wireOp",EDGE,"E81"),sQuery(id+"F0.wireOp",EDGE,"E82"),sQuery(id+"F0.wireOp",EDGE,"E83"),sQuery(id+"F0.wireOp",EDGE,"E84"),sQuery(id+"F0.wireOp",EDGE,"E85"),sQuery(id+"F0.wireOp",EDGE,"E86"),sQuery(id+"F0.wireOp",EDGE,"E87"),sQuery(id+"F0.wireOp",EDGE,"E88"),sQuery(id+"F0.wireOp",EDGE,"E89"),sQuery(id+"F0.wireOp",EDGE,"E90"),sQuery(id+"F0.wireOp",EDGE,"E91"),sQuery(id+"F0.wireOp",EDGE,"E92"),sQuery(id+"F0.wireOp",EDGE,"E93"),sQuery(id+"F0.wireOp",EDGE,"E94"),sQuery(id+"F0.wireOp",EDGE,"E95"),sQuery(id+"F0.wireOp",EDGE,"E96"),sQuery(id+"F0.wireOp",EDGE,"E97"),sQuery(id+"F0.wireOp",EDGE,"E98"),sQuery(id+"F0.wireOp",EDGE,"E99"),sQuery(id+"F0.wireOp",EDGE,"E100"),sQuery(id+"F0.wireOp",EDGE,"E101"),sQuery(id+"F0.wireOp",EDGE,"E102"),sQuery(id+"F0.wireOp",EDGE,"E103"),sQuery(id+"F0.wireOp",EDGE,"E104"),sQuery(id+"F0.wireOp",EDGE,"E105"),sQuery(id+"F0.wireOp",EDGE,"E106"),sQuery(id+"F0.wireOp",EDGE,"E107"),sQuery(id+"F0.wireOp",EDGE,"E108"),sQuery(id+"F0.wireOp",EDGE,"E109"),sQuery(id+"F0.wireOp",EDGE,"E110"),sQuery(id+"F0.wireOp",EDGE,"E111"),sQuery(id+"F0.wireOp",EDGE,"E112"),sQuery(id+"F0.wireOp",EDGE,"E113"),sQuery(id+"F0.wireOp",EDGE,"E114"),sQuery(id+"F0.wireOp",EDGE,"E115"),sQuery(id+"F0.wireOp",EDGE,"E116"),sQuery(id+"F0.wireOp",EDGE,"E117"),sQuery(id+"F0.wireOp",EDGE,"E118"),sQuery(id+"F0.wireOp",EDGE,"E119"),sQuery(id+"F0.wireOp",EDGE,"E120"),sQuery(id+"F0.wireOp",EDGE,"E121"),sQuery(id+"F0.wireOp",EDGE,"E122"),sQuery(id+"F0.wireOp",EDGE,"E123"),sQuery(id+"F0.wireOp",EDGE,"E124"),sQuery(id+"F0.wireOp",EDGE,"E125"),sQuery(id+"F0.wireOp",EDGE,"E126"),sQuery(id+"F0.wireOp",EDGE,"E127"),sQuery(id+"F0.wireOp",EDGE,"E128"),sQuery(id+"F0.wireOp",EDGE,"E129"),sQuery(id+"F0.wireOp",EDGE,"E130"),sQuery(id+"F0.wireOp",EDGE,"E131"),sQuery(id+"F0.wireOp",EDGE,"E132"),sQuery(id+"F0.wireOp",EDGE,"E133"),sQuery(id+"F0.wireOp",EDGE,"E134"),sQuery(id+"F0.wireOp",EDGE,"E135"),sQuery(id+"F0.wireOp",EDGE,"E136"),sQuery(id+"F0.wireOp",EDGE,"E137"),sQuery(id+"F0.wireOp",EDGE,"E138"),sQuery(id+"F0.wireOp",EDGE,"E139"),sQuery(id+"F0.wireOp",EDGE,"E140"),sQuery(id+"F0.wireOp",EDGE,"E141"),sQuery(id+"F0.wireOp",EDGE,"E142"),sQuery(id+"F0.wireOp",EDGE,"E143"),sQuery(id+"F0.wireOp",EDGE,"E144"),sQuery(id+"F0.wireOp",EDGE,"E145"),sQuery(id+"F0.wireOp",EDGE,"E146"),sQuery(id+"F0.wireOp",EDGE,"E147"),sQuery(id+"F0.wireOp",EDGE,"E148"),sQuery(id+"F0.wireOp",EDGE,"E149"),sQuery(id+"F0.wireOp",EDGE,"E150"),sQuery(id+"F0.wireOp",EDGE,"E151"),sQuery(id+"F0.wireOp",EDGE,"E152"),sQuery(id+"F0.wireOp",EDGE,"E153"),sQuery(id+"F0.wireOp",EDGE,"E154"),sQuery(id+"F0.wireOp",EDGE,"E155"),sQuery(id+"F0.wireOp",EDGE,"E156"),sQuery(id+"F0.wireOp",EDGE,"E157"),sQuery(id+"F0.wireOp",EDGE,"E158"),sQuery(id+"F0.wireOp",EDGE,"E159"),sQuery(id+"F0.wireOp",EDGE,"E160"),sQuery(id+"F0.wireOp",EDGE,"E161"),sQuery(id+"F0.wireOp",EDGE,"E162"),sQuery(id+"F0.wireOp",EDGE,"E163"),sQuery(id+"F0.wireOp",EDGE,"E164"),sQuery(id+"F0.wireOp",EDGE,"E165"),sQuery(id+"F0.wireOp",EDGE,"E166"),sQuery(id+"F0.wireOp",EDGE,"E167"),sQuery(id+"F0.wireOp",EDGE,"E168"),sQuery(id+"F0.wireOp",EDGE,"E169"),sQuery(id+"F0.wireOp",EDGE,"E170"),sQuery(id+"F0.wireOp",EDGE,"E171"),sQuery(id+"F0.wireOp",EDGE,"E172"),sQuery(id+"F0.wireOp",EDGE,"E173"),sQuery(id+"F0.wireOp",EDGE,"E174"),sQuery(id+"F0.wireOp",EDGE,"E175"),sQuery(id+"F0.wireOp",EDGE,"E176"),sQuery(id+"F0.wireOp",EDGE,"E177"),sQuery(id+"F0.wireOp",EDGE,"E178"),sQuery(id+"F0.wireOp",EDGE,"E179"),sQuery(id+"F0.wireOp",EDGE,"E180"),sQuery(id+"F0.wireOp",EDGE,"E181"),sQuery(id+"F0.wireOp",EDGE,"E182"),sQuery(id+"F0.wireOp",EDGE,"E183"),sQuery(id+"F0.wireOp",EDGE,"E184"),sQuery(id+"F0.wireOp",EDGE,"E185"),sQuery(id+"F0.wireOp",EDGE,"E186"),sQuery(id+"F0.wireOp",EDGE,"E187"),sQuery(id+"F0.wireOp",EDGE,"E188"),sQuery(id+"F0.wireOp",EDGE,"E189"),sQuery(id+"F0.wireOp",EDGE,"E190"),sQuery(id+"F0.wireOp",EDGE,"E191"),sQuery(id+"F0.wireOp",EDGE,"E192"),sQuery(id+"F0.wireOp",EDGE,"E193"),sQuery(id+"F0.wireOp",EDGE,"E194"),sQuery(id+"F0.wireOp",EDGE,"E195"),sQuery(id+"F0.wireOp",EDGE,"E196"),sQuery(id+"F0.wireOp",EDGE,"E197"),sQuery(id+"F0.wireOp",EDGE,"E198"),sQuery(id+"F0.wireOp",EDGE,"E199"),sQuery(id+"F0.wireOp",EDGE,"E200"),sQuery(id+"F0.wireOp",EDGE,"E201"),sQuery(id+"F0.wireOp",EDGE,"E202"),sQuery(id+"F0.wireOp",EDGE,"E203"),sQuery(id+"F0.wireOp",EDGE,"E204"),sQuery(id+"F0.wireOp",EDGE,"E205"),sQuery(id+"F0.wireOp",EDGE,"E206"),sQuery(id+"F0.wireOp",EDGE,"E207"),sQuery(id+"F0.wireOp",EDGE,"E208"),sQuery(id+"F0.wireOp",EDGE,"E209"),sQuery(id+"F0.wireOp",EDGE,"E210"),sQuery(id+"F0.wireOp",EDGE,"E211"),sQuery(id+"F0.wireOp",EDGE,"E212"),sQuery(id+"F0.wireOp",EDGE,"E213"),sQuery(id+"F0.wireOp",EDGE,"E214"),sQuery(id+"F0.wireOp",EDGE,"E215"),sQuery(id+"F0.wireOp",EDGE,"E216"),sQuery(id+"F0.wireOp",EDGE,"E217"),sQuery(id+"F0.wireOp",EDGE,"E218"),sQuery(id+"F0.wireOp",EDGE,"E219"),sQuery(id+"F0.wireOp",EDGE,"E220"),sQuery(id+"F0.wireOp",EDGE,"E221"),sQuery(id+"F0.wireOp",EDGE,"E222"),sQuery(id+"F0.wireOp",EDGE,"E223"),sQuery(id+"F0.wireOp",EDGE,"E224"),sQuery(id+"F0.wireOp",EDGE,"E225"),sQuery(id+"F0.wireOp",EDGE,"E226"),sQuery(id+"F0.wireOp",EDGE,"E227"),sQuery(id+"F0.wireOp",EDGE,"E228"),sQuery(id+"F0.wireOp",EDGE,"E229"),sQuery(id+"F0.wireOp",EDGE,"E230"),sQuery(id+"F0.wireOp",EDGE,"E231"),sQuery(id+"F0.wireOp",EDGE,"E232"),sQuery(id+"F0.wireOp",EDGE,"E233"),sQuery(id+"F0.wireOp",EDGE,"E234"),sQuery(id+"F0.wireOp",EDGE,"E235"),sQuery(id+"F0.wireOp",EDGE,"E236"),sQuery(id+"F0.wireOp",EDGE,"E237"),sQuery(id+"F0.wireOp",EDGE,"E238"),sQuery(id+"F0.wireOp",EDGE,"E239"),sQuery(id+"F0.wireOp",EDGE,"E240"),sQuery(id+"F0.wireOp",EDGE,"E241"),sQuery(id+"F0.wireOp",EDGE,"E242"),sQuery(id+"F0.wireOp",EDGE,"E243"),sQuery(id+"F0.wireOp",EDGE,"E244"),sQuery(id+"F0.wireOp",EDGE,"E245"),sQuery(id+"F0.wireOp",EDGE,"E246"),sQuery(id+"F0.wireOp",EDGE,"E247"),sQuery(id+"F0.wireOp",EDGE,"E248"),sQuery(id+"F0.wireOp",EDGE,"E249"),sQuery(id+"F0.wireOp",EDGE,"E250"),sQuery(id+"F0.wireOp",EDGE,"E251"),sQuery(id+"F0.wireOp",EDGE,"E252"),sQuery(id+"F0.wireOp",EDGE,"E253"),sQuery(id+"F0.wireOp",EDGE,"E254"),sQuery(id+"F0.wireOp",EDGE,"E255"),sQuery(id+"F0.wireOp",EDGE,"E256"),sQuery(id+"F0.wireOp",EDGE,"E257"),sQuery(id+"F0.wireOp",EDGE,"E258"),sQuery(id+"F0.wireOp",EDGE,"E259"),sQuery(id+"F0.wireOp",EDGE,"E260"),sQuery(id+"F0.wireOp",EDGE,"E261"),sQuery(id+"F0.wireOp",EDGE,"E262"),sQuery(id+"F0.wireOp",EDGE,"E263"),sQuery(id+"F0.wireOp",EDGE,"E264"),sQuery(id+"F0.wireOp",EDGE,"E265"),sQuery(id+"F0.wireOp",EDGE,"E266"),sQuery(id+"F0.wireOp",EDGE,"E267"),sQuery(id+"F0.wireOp",EDGE,"E268"),sQuery(id+"F0.wireOp",EDGE,"E269"),sQuery(id+"F0.wireOp",EDGE,"E270"),sQuery(id+"F0.wireOp",EDGE,"E271"),sQuery(id+"F0.wireOp",EDGE,"E272"),sQuery(id+"F0.wireOp",EDGE,"E273"),sQuery(id+"F0.wireOp",EDGE,"E274"),sQuery(id+"F0.wireOp",EDGE,"E275"),sQuery(id+"F0.wireOp",EDGE,"E276"),sQuery(id+"F0.wireOp",EDGE,"E277"),sQuery(id+"F0.wireOp",EDGE,"E278"),sQuery(id+"F0.wireOp",EDGE,"E279"),sQuery(id+"F0.wireOp",EDGE,"E280"),sQuery(id+"F0.wireOp",EDGE,"E281"),sQuery(id+"F0.wireOp",EDGE,"E282"),sQuery(id+"F0.wireOp",EDGE,"E283"),sQuery(id+"F0.wireOp",EDGE,"E284"),sQuery(id+"F0.wireOp",EDGE,"E285"),sQuery(id+"F0.wireOp",EDGE,"E286"),sQuery(id+"F0.wireOp",EDGE,"E287"),sQuery(id+"F0.wireOp",EDGE,"E288"),sQuery(id+"F0.wireOp",EDGE,"E289"),sQuery(id+"F0.wireOp",EDGE,"E290"),sQuery(id+"F0.wireOp",EDGE,"E291"),sQuery(id+"F0.wireOp",EDGE,"E292"),sQuery(id+"F0.wireOp",EDGE,"E293"),sQuery(id+"F0.wireOp",EDGE,"E294"),sQuery(id+"F0.wireOp",EDGE,"E295"),sQuery(id+"F0.wireOp",EDGE,"E296"),sQuery(id+"F0.wireOp",EDGE,"E297"),sQuery(id+"F0.wireOp",EDGE,"E298"),sQuery(id+"F0.wireOp",EDGE,"E299"),sQuery(id+"F0.wireOp",EDGE,"E300"),sQuery(id+"F0.wireOp",EDGE,"E301"),sQuery(id+"F0.wireOp",EDGE,"E302"),sQuery(id+"F0.wireOp",EDGE,"E303"),sQuery(id+"F0.wireOp",EDGE,"E304"),sQuery(id+"F0.wireOp",EDGE,"E305"),sQuery(id+"F0.wireOp",EDGE,"E306"),sQuery(id+"F0.wireOp",EDGE,"E307"),sQuery(id+"F0.wireOp",EDGE,"E308"),sQuery(id+"F0.wireOp",EDGE,"E309"),sQuery(id+"F0.wireOp",EDGE,"E310"),sQuery(id+"F0.wireOp",EDGE,"E311"),sQuery(id+"F0.wireOp",EDGE,"E312"),sQuery(id+"F0.wireOp",EDGE,"E313"),sQuery(id+"F0.wireOp",EDGE,"E314"),sQuery(id+"F0.wireOp",EDGE,"E315"),sQuery(id+"F0.wireOp",EDGE,"E316"),sQuery(id+"F0.wireOp",EDGE,"E317"),sQuery(id+"F0.wireOp",EDGE,"E318"),sQuery(id+"F0.wireOp",EDGE,"E319"),sQuery(id+"F0.wireOp",EDGE,"E320"),sQuery(id+"F0.wireOp",EDGE,"E321"),sQuery(id+"F0.wireOp",EDGE,"E322"),sQuery(id+"F0.wireOp",EDGE,"E323"),sQuery(id+"F0.wireOp",EDGE,"E324"),sQuery(id+"F0.wireOp",EDGE,"E325"),sQuery(id+"F0.wireOp",EDGE,"E326"),sQuery(id+"F0.wireOp",EDGE,"E327"),sQuery(id+"F0.wireOp",EDGE,"E328"),sQuery(id+"F0.wireOp",EDGE,"E329"),sQuery(id+"F0.wireOp",EDGE,"E330"),sQuery(id+"F0.wireOp",EDGE,"E331"),sQuery(id+"F0.wireOp",EDGE,"E332"),sQuery(id+"F0.wireOp",EDGE,"E333"),sQuery(id+"F0.wireOp",EDGE,"E334"),sQuery(id+"F0.wireOp",EDGE,"E335"),sQuery(id+"F0.wireOp",EDGE,"E336"),sQuery(id+"F0.wireOp",EDGE,"E337"),sQuery(id+"F0.wireOp",EDGE,"E338"),sQuery(id+"F0.wireOp",EDGE,"E339"),sQuery(id+"F0.wireOp",EDGE,"E340"),sQuery(id+"F0.wireOp",EDGE,"E341"),sQuery(id+"F0.wireOp",EDGE,"E342"),sQuery(id+"F0.wireOp",EDGE,"E343"),sQuery(id+"F0.wireOp",EDGE,"E344"),sQuery(id+"F0.wireOp",EDGE,"E345"),sQuery(id+"F0.wireOp",EDGE,"E346"),sQuery(id+"F0.wireOp",EDGE,"E347"),sQuery(id+"F0.wireOp",EDGE,"E348"),sQuery(id+"F0.wireOp",EDGE,"E349"),sQuery(id+"F0.wireOp",EDGE,"E350"),sQuery(id+"F0.wireOp",EDGE,"E351"),sQuery(id+"F0.wireOp",EDGE,"E352"),sQuery(id+"F0.wireOp",EDGE,"E353"),sQuery(id+"F0.wireOp",EDGE,"E354"),sQuery(id+"F0.wireOp",EDGE,"E355"),sQuery(id+"F0.wireOp",EDGE,"E356"),sQuery(id+"F0.wireOp",EDGE,"E357"),sQuery(id+"F0.wireOp",EDGE,"E358"),sQuery(id+"F0.wireOp",EDGE,"E359"),sQuery(id+"F0.wireOp",EDGE,"E360"),sQuery(id+"F0.wireOp",EDGE,"E361"),sQuery(id+"F0.wireOp",EDGE,"E362"),sQuery(id+"F0.wireOp",EDGE,"E363"),sQuery(id+"F0.wireOp",EDGE,"E364"),sQuery(id+"F0.wireOp",EDGE,"E365"),sQuery(id+"F0.wireOp",EDGE,"E366"),sQuery(id+"F0.wireOp",EDGE,"E367"),sQuery(id+"F0.wireOp",EDGE,"E368"),sQuery(id+"F0.wireOp",EDGE,"E369"),sQuery(id+"F0.wireOp",EDGE,"E370"),sQuery(id+"F0.wireOp",EDGE,"E371"),sQuery(id+"F0.wireOp",EDGE,"E372"),sQuery(id+"F0.wireOp",EDGE,"E373"),sQuery(id+"F0.wireOp",EDGE,"E374"),sQuery(id+"F0.wireOp",EDGE,"E375"),sQuery(id+"F0.wireOp",EDGE,"E376"),sQuery(id+"F0.wireOp",EDGE,"E377"),sQuery(id+"F0.wireOp",EDGE,"E378"),sQuery(id+"F0.wireOp",EDGE,"E379"),sQuery(id+"F0.wireOp",EDGE,"E380"),sQuery(id+"F0.wireOp",EDGE,"E381"),sQuery(id+"F0.wireOp",EDGE,"E382"),sQuery(id+"F0.wireOp",EDGE,"E383"),sQuery(id+"F0.wireOp",EDGE,"E384"),sQuery(id+"F0.wireOp",EDGE,"E385"),sQuery(id+"F0.wireOp",EDGE,"E386"),sQuery(id+"F0.wireOp",EDGE,"E387"),sQuery(id+"F0.wireOp",EDGE,"E388"),sQuery(id+"F0.wireOp",EDGE,"E389"),sQuery(id+"F0.wireOp",EDGE,"E390"),sQuery(id+"F0.wireOp",EDGE,"E391"),sQuery(id+"F0.wireOp",EDGE,"E392"),sQuery(id+"F0.wireOp",EDGE,"E393"),sQuery(id+"F0.wireOp",EDGE,"E394"),sQuery(id+"F0.wireOp",EDGE,"E395")])],"isStart":false});
            var sketch = newSketch(context, id + "F2", { "sketchPlane" : qUnion([Q0])});
            skCircle(sketch, "E396", {"center": v(0, 0) * mm, "radius": 1.5 * mm});
            skSolve(sketch);
        }
        {
            var Q0;
            Q0 = qSketchRegion(id + "F2", true);
            extrude(context, id + "F3", {"entities" : qUnion([Q0]), "operationType" : NewBodyOperationType.REMOVE, "endBound" : BoundingType.UP_TO_NEXT, "oppositeDirection" : true, "depth" : 25 * mm, "offsetDistance" : 25 * mm});
        }
    });
